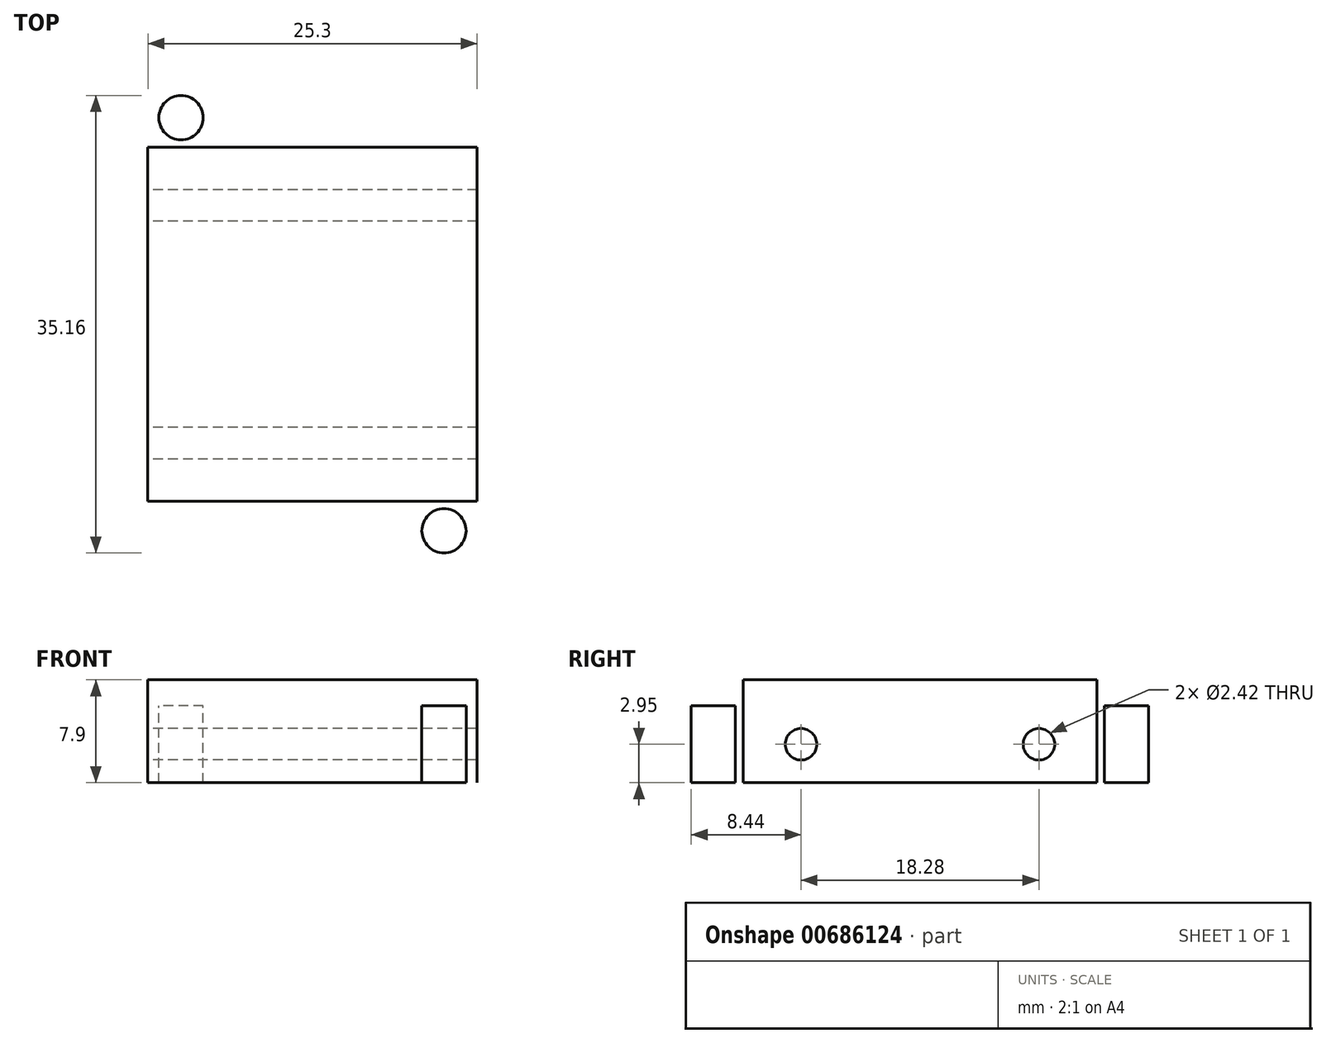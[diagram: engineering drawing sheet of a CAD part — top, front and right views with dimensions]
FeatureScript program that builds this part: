
annotation { "Feature Type Name" : "Feature", "Feature Type Description" : "" }
export const myFeature = defineFeature(function(context is Context, id is Id, definition is map)
    precondition{}
    {
        {
            var Q0;
            Q0=qCreatedBy(makeId("Front.planeOp"),FACE);
            var sketch = newSketch(context, id + "F0", { "sketchPlane" : qUnion([Q0])});
            skLineSegment(sketch, "E0.bottom", {"start": v(-9.01, 5.9) * mm, "end": v(16.29, 5.9) * mm});
            skLineSegment(sketch, "E0.top", {"start": v(-9.01, 0) * mm, "end": v(16.29, 0) * mm});
            skLineSegment(sketch, "E0.left", {"start": v(-9.01, 5.9) * mm, "end": v(-9.01, 0) * mm});
            skLineSegment(sketch, "E0.right", {"start": v(16.29, 5.9) * mm, "end": v(16.29, 0) * mm});
            skLineSegment(sketch, "E1.bottom", {"start": v(6.22, -3.35) * mm, "end": v(6.14, -3.35) * mm});
            skLineSegment(sketch, "E1.top", {"start": v(6.22, 0) * mm, "end": v(1.06, 0) * mm});
            skLineSegment(sketch, "E1.left", {"start": v(6.22, -3.35) * mm, "end": v(6.22, 0) * mm});
            skLineSegment(sketch, "E1.right", {"start": v(1.06, -3.35) * mm, "end": v(1.06, 0) * mm});
            skPoint(sketch, "E2", {"position": v(3.64, 0) * mm});
            skLineSegment(sketch, "E3", {"start": v(3.64, 5.9) * mm, "end": v(3.64, -23.7) * mm, "construction": true});
            skPoint(sketch, "E4", {"position": v(3.64, -2.85) * mm});
            skLineSegment(sketch, "E5", {"start": v(1.14, -3.35) * mm, "end": v(1.06, -3.35) * mm});
            skLineSegment(sketch, "E6", {"start": v(6.14, -3.35) * mm, "end": v(1.14, -3.35) * mm, "construction": true});
            skArc(sketch, "E7", {"start": v(1.14, -3.35) * mm, "mid": v(3.64, -5.85) * mm, "end": v(6.14, -3.35) * mm, "construction": true});
            skArc(sketch, "E8", {"start": v(6.14, -3.35) * mm, "mid": v(3.64, -0.85) * mm, "end": v(1.14, -3.35) * mm});
            skSolve(sketch);
        }
        {
            var Q0;
            Q0=makeQuery(id+"F0.imprint","IMPRINT",FACE,{"disambiguationData":[TD([[makeQuery(id+"F0.imprint","IMPRINT",EDGE,{"derivedFrom":sQuery(id+"F0.wireOp",EDGE,"E0.bottom")}),-1.0]])]});
            var Q1;
            Q1=makeQuery(id+"F0.imprint","IMPRINT",FACE,{"disambiguationData":[TD([[makeQuery(id+"F0.imprint","IMPRINT",EDGE,{"derivedFrom":sQuery(id+"F0.wireOp",EDGE,"E1.bottom")}),-1.0]])]});
            extrude(context, id + "F1", {"entities" : qUnion([Q0, Q1]), "endBound" : BoundingType.SYMMETRIC, "depth" : 41.5 * mm, "offsetDistance" : 25 * mm});
        }
        {
            var Q0;
            Q0=makeQuery(id+"F1.opExtrude","SWEPT_FACE",FACE,{"disambiguationData":[OSD([sQuery(id+"F0.wireOp",EDGE,"E0.bottom")])]});
            var sketch = newSketch(context, id + "F2", { "sketchPlane" : qUnion([Q0])});
            skLineSegment(sketch, "E9", {"start": v(16.29, 13.6) * mm, "end": v(-9.01, 13.6) * mm});
            skLineSegment(sketch, "E10", {"start": v(0, 0) * mm, "end": v(16.29, 0) * mm, "construction": true});
            skLineSegment(sketch, "E11.MirrorCS", {"start": v(16.29, -13.6) * mm, "end": v(-9.01, -13.6) * mm});
            skLineSegment(sketch, "E12", {"start": v(16.29, 14.18) * mm, "end": v(-9.01, 14.18) * mm, "construction": true});
            skLineSegment(sketch, "E13.MirrorCS", {"start": v(16.29, -14.18) * mm, "end": v(-9.01, -14.18) * mm, "construction": true});
            skLineSegment(sketch, "E14", {"start": v(12.04, 20.75) * mm, "end": v(12.04, -20.75) * mm, "construction": true});
            skPoint(sketch, "E15", {"position": v(3.64, -20.75) * mm});
            skLineSegment(sketch, "E16", {"start": v(3.64, -20.75) * mm, "end": v(3.64, 0) * mm, "construction": true});
            skLineSegment(sketch, "E17.MirrorCS", {"start": v(-4.76, 20.75) * mm, "end": v(-4.76, -20.75) * mm, "construction": true});
            skCircle(sketch, "E18", {"center": v(-6.46, -15.88) * mm, "radius": 1.7 * mm});
            skCircle(sketch, "E19.MirrorC", {"center": v(13.74, -15.88) * mm, "radius": 1.7 * mm});
            skCircle(sketch, "E20.MirrorC", {"center": v(-6.46, 15.88) * mm, "radius": 1.7 * mm});
            skCircle(sketch, "E21.MirrorC", {"center": v(13.74, 15.88) * mm, "radius": 1.7 * mm});
            skSolve(sketch);
        }
        {
            var Q0;
            {var subQ0=sQuery(id+"F2.wireOp",EDGE,"E9");Q0=makeQuery(id+"F2.imprint","IMPRINT",FACE,{"disambiguationData":[TD([[makeQuery(id+"F2.imprint","IMPRINT",EDGE,{"derivedFrom":subQ0}),1.0]])]});}
            extrude(context, id + "F3", {"entities" : qUnion([Q0]), "operationType" : NewBodyOperationType.ADD, "depth" : 2 * mm, "offsetDistance" : 25 * mm});
        }
        {
            var Q0;
            Q0=makeQuery(id+"F2.imprint","IMPRINT",FACE,{"disambiguationData":[TD([[makeQuery(id+"F2.imprint","IMPRINT",EDGE,{"derivedFrom":sQuery(id+"F2.wireOp",EDGE,"E21.MirrorC")}),1.0]])]});
            var Q1;
            Q1=makeQuery(id+"F2.imprint","IMPRINT",FACE,{"disambiguationData":[TD([[makeQuery(id+"F2.imprint","IMPRINT",EDGE,{"derivedFrom":sQuery(id+"F2.wireOp",EDGE,"E20.MirrorC")}),-1.0]])]});
            var Q2;
            Q2=makeQuery(id+"F2.imprint","IMPRINT",FACE,{"disambiguationData":[TD([[makeQuery(id+"F2.imprint","IMPRINT",EDGE,{"derivedFrom":sQuery(id+"F2.wireOp",EDGE,"E18")}),1.0]])]});
            var Q3;
            Q3=makeQuery(id+"F2.imprint","IMPRINT",FACE,{"disambiguationData":[TD([[makeQuery(id+"F2.imprint","IMPRINT",EDGE,{"derivedFrom":sQuery(id+"F2.wireOp",EDGE,"E19.MirrorC")}),-1.0]])]});
            extrude(context, id + "F4", {"entities" : qUnion([Q0, Q1, Q2, Q3]), "operationType" : NewBodyOperationType.REMOVE, "endBound" : BoundingType.THROUGH_ALL, "oppositeDirection" : true, "depth" : 25 * mm, "offsetDistance" : 25 * mm});
        }
        {
            var Q0;
            {var subQ0=sQuery(id+"F0.wireOp",EDGE,"E0.left");Q0=makeQuery(id+"F3.boolean.opBoolean","MERGE",FACE,{"derivedFrom":[makeQuery(id+"F1.opExtrude","SWEPT_FACE",FACE,{"disambiguationData":[OSD([subQ0])]}),makeQuery(id+"F3.opExtrude","SWEPT_FACE",FACE,{"disambiguationData":[OSD([sQuery(id+"F0.wireOp",EDGE,"E0.bottom"),subQ0])]})]});}
            var sketch = newSketch(context, id + "F5", { "sketchPlane" : qUnion([Q0])});
            skLineSegment(sketch, "E22.0.0", {"start": v(-20.75, 0) * mm, "end": v(-20.75, -3.35) * mm, "construction": true});
            skLineSegment(sketch, "E22.0.1", {"start": v(-20.75, -3.35) * mm, "end": v(20.75, -3.35) * mm, "construction": true});
            skLineSegment(sketch, "E22.0.2", {"start": v(20.75, -3.35) * mm, "end": v(20.75, 0) * mm, "construction": true});
            skLineSegment(sketch, "E22.0.3", {"start": v(20.75, 0) * mm, "end": v(-20.75, 0) * mm, "construction": true});
            skLineSegment(sketch, "E23", {"start": v(-20.75, 2.95) * mm, "end": v(20.75, 2.95) * mm, "construction": true});
            skPoint(sketch, "E24", {"position": v(-10.35, 2.95) * mm});
            skPoint(sketch, "E25", {"position": v(10.35, 2.95) * mm});
            skCircle(sketch, "E26", {"center": v(-9.14, 2.95) * mm, "radius": 1.21 * mm});
            skCircle(sketch, "E27", {"center": v(9.14, 2.95) * mm, "radius": 1.21 * mm});
            skLineSegment(sketch, "E28.bottom", {"start": v(-13.85, 0) * mm, "end": v(13.85, 0) * mm});
            skLineSegment(sketch, "E28.top", {"start": v(-13.85, -3.35) * mm, "end": v(13.85, -3.35) * mm});
            skLineSegment(sketch, "E28.left", {"start": v(-13.85, 0) * mm, "end": v(-13.85, -3.35) * mm});
            skLineSegment(sketch, "E28.right", {"start": v(13.85, 0) * mm, "end": v(13.85, -3.35) * mm});
            skSolve(sketch);
        }
        {
            var Q0;
            Q0=makeQuery(id+"F5.imprint","IMPRINT",FACE,{"disambiguationData":[TD([[makeQuery(id+"F5.imprint","IMPRINT",EDGE,{"derivedFrom":sQuery(id+"F5.wireOp",EDGE,"E28.bottom")}),1.0]])]});
            var Q1;
            Q1=makeQuery(id+"F5.imprint","IMPRINT",FACE,{"disambiguationData":[TD([[makeQuery(id+"F5.imprint","IMPRINT",EDGE,{"derivedFrom":sQuery(id+"F5.wireOp",EDGE,"E27")}),1.0]])]});
            var Q2;
            Q2=makeQuery(id+"F5.imprint","IMPRINT",FACE,{"disambiguationData":[TD([[makeQuery(id+"F5.imprint","IMPRINT",EDGE,{"derivedFrom":sQuery(id+"F5.wireOp",EDGE,"E26")}),1.0]])]});
            extrude(context, id + "F6", {"entities" : qUnion([Q0, Q1, Q2]), "operationType" : NewBodyOperationType.REMOVE, "endBound" : BoundingType.THROUGH_ALL, "oppositeDirection" : true, "depth" : 25 * mm, "offsetDistance" : 25 * mm});
        }
    });
